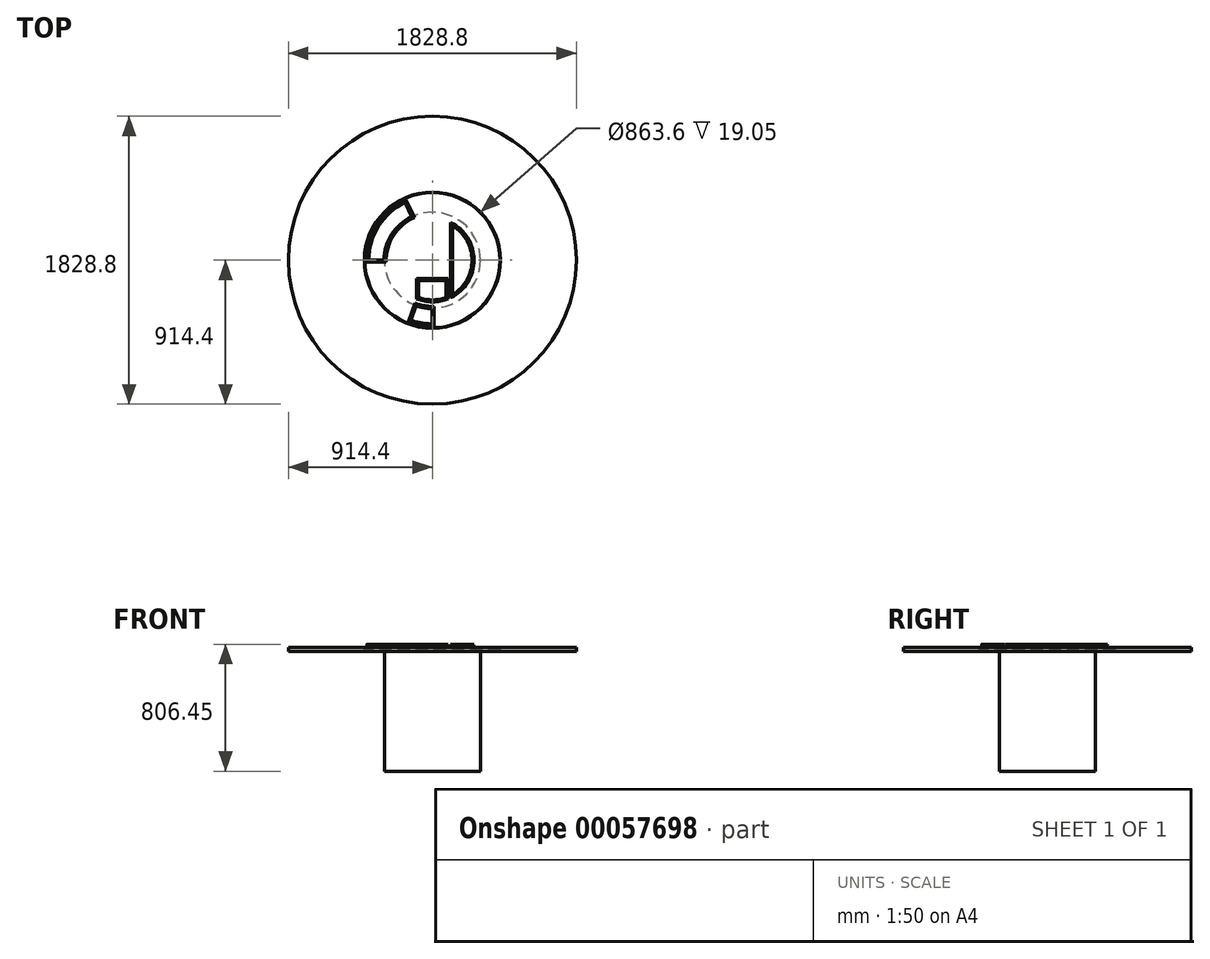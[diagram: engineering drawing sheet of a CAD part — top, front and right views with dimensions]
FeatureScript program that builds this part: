
annotation { "Feature Type Name" : "Feature", "Feature Type Description" : "" }
export const myFeature = defineFeature(function(context is Context, id is Id, definition is map)
    precondition{}
    {
        {
            var Q0;
            Q0=qCreatedBy(makeId("Top.planeOp"),FACE);
            var sketch = newSketch(context, id + "F0", { "sketchPlane" : qUnion([Q0])});
            skCircle(sketch, "E0", {"center": v(0, 0) * mm, "radius": 914.4 * mm});
            skSolve(sketch);
        }
        {
            var Q0;
            Q0 = qSketchRegion(id + "F0", true);
            extrude(context, id + "F1", {"entities" : qUnion([Q0]), "depth" : 25.4 * mm});
        }
        {
            var Q0;
            Q0=makeQuery(id+"F1.opExtrude","CAP_FACE",FACE,{"disambiguationData":[OSD([sQuery(id+"F0.wireOp",EDGE,"E0")])],"isStart":false});
            var sketch = newSketch(context, id + "F2", { "sketchPlane" : qUnion([Q0])});
            skCircle(sketch, "E1", {"center": v(0, 0) * mm, "radius": 431.8 * mm});
            skSolve(sketch);
        }
        {
            var Q0;
            Q0 = qSketchRegion(id + "F2", true);
            extrude(context, id + "F3", {"entities" : qUnion([Q0]), "operationType" : NewBodyOperationType.REMOVE, "oppositeDirection" : true, "depth" : 19.05 * mm});
        }
        {
            var Q0;
            Q0=makeQuery(id+"F3.boolean.opBoolean","COPY",FACE,{"derivedFrom":makeQuery(id+"F3.opExtrude","CAP_FACE",FACE,{"disambiguationData":[OSD([sQuery(id+"F2.wireOp",EDGE,"E1")])],"isStart":false})});
            var sketch = newSketch(context, id + "F4", { "sketchPlane" : qUnion([Q0])});
            skCircle(sketch, "E2", {"center": v(0, 0) * mm, "radius": 428.63 * mm});
            skSolve(sketch);
        }
        {
            var Q0;
            Q0 = qSketchRegion(id + "F4", true);
            extrude(context, id + "F5", {"entities" : qUnion([Q0]), "depth" : 19.05 * mm});
        }
        {
            var Q0;
            Q0=makeQuery(id+"F1.opExtrude","CAP_FACE",FACE,{"disambiguationData":[OSD([sQuery(id+"F0.wireOp",EDGE,"E0")])],"isStart":true});
            var sketch = newSketch(context, id + "F6", { "sketchPlane" : qUnion([Q0])});
            skCircle(sketch, "E3", {"center": v(0, 0) * mm, "radius": 304.8 * mm});
            skSolve(sketch);
        }
        {
            var Q0;
            Q0 = qSketchRegion(id + "F6", true);
            extrude(context, id + "F7", {"entities" : qUnion([Q0]), "operationType" : NewBodyOperationType.ADD, "depth" : 762 * mm});
        }
        {
            var Q0;
            Q0=makeQuery(id+"F5.opExtrude","CAP_FACE",FACE,{"disambiguationData":[OSD([sQuery(id+"F4.wireOp",EDGE,"E2")])],"isStart":false});
            var sketch = newSketch(context, id + "F8", { "sketchPlane" : qUnion([Q0])});
            skArc(sketch, "E4", {"start": v(-406.4, 0) * mm, "mid": v(-342.75, 218.36) * mm, "end": v(-171.75, 368.32) * mm});
            skArc(sketch, "E5", {"start": v(-304.8, 0) * mm, "mid": v(-257.07, 163.77) * mm, "end": v(-128.81, 276.24) * mm});
            skLineSegment(sketch, "E6", {"start": v(-406.4, 0) * mm, "end": v(-304.8, 0) * mm});
            skLineSegment(sketch, "E7", {"start": v(-171.75, 368.32) * mm, "end": v(-128.81, 276.24) * mm});
            skSolve(sketch);
        }
        {
            var Q0;
            Q0 = qSketchRegion(id + "F8", true);
            extrude(context, id + "F9", {"entities" : qUnion([Q0]), "depth" : 19.05 * mm, "hasDraft" : true, "draftAngle" : 30 * degree});
        }
        {
            var Q0;
            Q0=makeQuery(id+"F9.opExtrude","CAP_FACE",FACE,{"disambiguationData":[OSD([sQuery(id+"F8.wireOp",EDGE,"affvSIiy-0v5L-dxoC-5kUw-lE1J0QHg8Nh6"),sQuery(id+"F8.wireOp",EDGE,"1R9Mnhxt-jNVk-8FeJ-3YnE-667WEw5VwUla"),sQuery(id+"F8.wireOp",EDGE,"6b6d8798-cfd3-4132-89cb-ca773a154ac6.trimOffspring"),sQuery(id+"F8.wireOp",EDGE,"775797dd-1884-4ee2-b150-e50d2a7a3543.trimOffspring")])],"isStart":false});
            var Q1;
            Q1=makeQuery(id+"F9.opExtrude","CAP_FACE",FACE,{"disambiguationData":[OSD([sQuery(id+"F8.wireOp",EDGE,"E4"),sQuery(id+"F8.wireOp",EDGE,"E5"),sQuery(id+"F8.wireOp",EDGE,"E6"),sQuery(id+"F8.wireOp",EDGE,"E7")])],"isStart":false});
            shell(context, id + "F10", {"entities" : qUnion([Q0, Q1]), "thickness" : 3.17 * mm});
        }
        {
            var Q0;
            Q0=makeQuery(id+"F5.opExtrude","CAP_FACE",FACE,{"disambiguationData":[OSD([sQuery(id+"F4.wireOp",EDGE,"E2")])],"isStart":false});
            var sketch = newSketch(context, id + "F11", { "sketchPlane" : qUnion([Q0])});
            skArc(sketch, "E8", {"start": v(0, -406.4) * mm, "mid": v(-70.57, -400.23) * mm, "end": v(-139, -381.9) * mm});
            skArc(sketch, "E9", {"start": v(0, -304.8) * mm, "mid": v(-52.93, -300.17) * mm, "end": v(-104.25, -286.42) * mm});
            skLineSegment(sketch, "E10", {"start": v(0, -406.4) * mm, "end": v(0, -304.8) * mm});
            skLineSegment(sketch, "E11", {"start": v(-139, -381.9) * mm, "end": v(-104.25, -286.42) * mm});
            skSolve(sketch);
        }
        {
            var Q0;
            Q0 = qSketchRegion(id + "F11", true);
            extrude(context, id + "F12", {"entities" : qUnion([Q0]), "depth" : 19.05 * mm, "hasDraft" : true, "draftAngle" : 30 * degree});
        }
        {
            var Q0;
            Q0=makeQuery(id+"F12.opExtrude","CAP_FACE",FACE,{"disambiguationData":[OSD([sQuery(id+"F11.wireOp",EDGE,"E8"),sQuery(id+"F11.wireOp",EDGE,"E9"),sQuery(id+"F11.wireOp",EDGE,"E10"),sQuery(id+"F11.wireOp",EDGE,"E11")])],"isStart":false});
            shell(context, id + "F13", {"entities" : qUnion([Q0]), "thickness" : 3.17 * mm});
        }
        {
            var Q0;
            Q0=makeQuery(id+"F5.opExtrude","CAP_FACE",FACE,{"disambiguationData":[OSD([sQuery(id+"F4.wireOp",EDGE,"E2")])],"isStart":false});
            var sketch = newSketch(context, id + "F14", { "sketchPlane" : qUnion([Q0])});
            skArc(sketch, "E12", {"start": v(127, 219.97) * mm, "mid": v(254, 0) * mm, "end": v(127, -219.97) * mm});
            skLineSegment(sketch, "E13", {"start": v(127, 0) * mm, "end": v(127, -219.97) * mm});
            skLineSegment(sketch, "E14", {"start": v(127, 0) * mm, "end": v(127, 219.97) * mm});
            skSolve(sketch);
        }
        {
            var Q0;
            Q0 = qSketchRegion(id + "F14", true);
            extrude(context, id + "F15", {"entities" : qUnion([Q0]), "depth" : 19.05 * mm, "hasDraft" : true, "draftAngle" : 30 * degree});
        }
        {
            var Q0;
            Q0=makeQuery(id+"F15.opExtrude","CAP_FACE",FACE,{"disambiguationData":[OSD([sQuery(id+"F14.wireOp",EDGE,"E12"),sQuery(id+"F14.wireOp",EDGE,"E13"),sQuery(id+"F14.wireOp",EDGE,"E14")])],"isStart":false});
            shell(context, id + "F16", {"entities" : qUnion([Q0]), "thickness" : 3.17 * mm});
        }
        {
            var Q0;
            Q0=makeQuery(id+"F5.opExtrude","CAP_FACE",FACE,{"disambiguationData":[OSD([sQuery(id+"F4.wireOp",EDGE,"E2")])],"isStart":false});
            var sketch = newSketch(context, id + "F17", { "sketchPlane" : qUnion([Q0])});
            skArc(sketch, "E15", {"start": v(88.9, -237.93) * mm, "mid": v(0, -254) * mm, "end": v(-88.9, -237.93) * mm});
            skLineSegment(sketch, "E16", {"start": v(88.9, -237.93) * mm, "end": v(88.9, -127) * mm});
            skLineSegment(sketch, "E17", {"start": v(88.9, -127) * mm, "end": v(-88.9, -127) * mm});
            skLineSegment(sketch, "E18", {"start": v(-88.9, -127) * mm, "end": v(-88.9, -237.93) * mm});
            skSolve(sketch);
        }
        {
            var Q0;
            Q0 = qSketchRegion(id + "F17", true);
            extrude(context, id + "F18", {"entities" : qUnion([Q0]), "depth" : 19.05 * mm, "hasDraft" : true, "draftAngle" : 30 * degree});
        }
        {
            var Q0;
            Q0=makeQuery(id+"F18.opExtrude","CAP_FACE",FACE,{"disambiguationData":[OSD([sQuery(id+"F17.wireOp",EDGE,"E15"),sQuery(id+"F17.wireOp",EDGE,"E16"),sQuery(id+"F17.wireOp",EDGE,"E17"),sQuery(id+"F17.wireOp",EDGE,"E18")])],"isStart":false});
            shell(context, id + "F19", {"entities" : qUnion([Q0]), "thickness" : 3.17 * mm});
        }
    });
